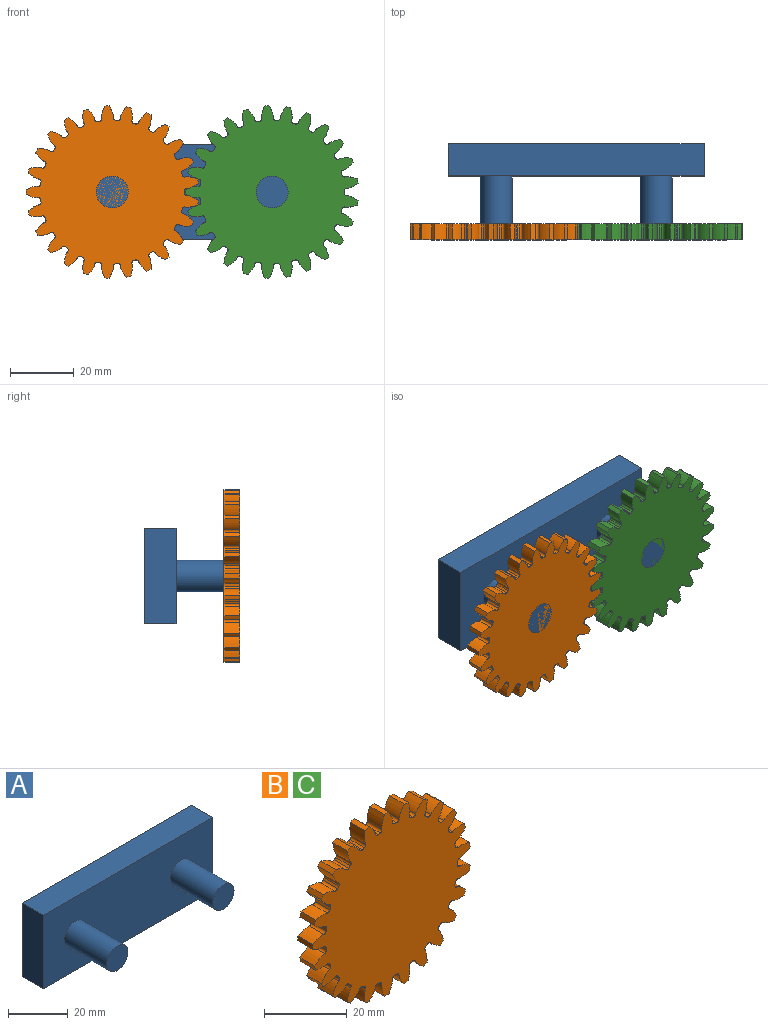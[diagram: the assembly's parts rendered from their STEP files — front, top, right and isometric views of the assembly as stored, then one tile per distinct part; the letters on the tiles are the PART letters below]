
ASSEMBLY  parts=3 mates=2
PART A: 10 faces, bbox 80x30x30 mm
  f0: plane 80x10mm, normal (0,0,1), area 800mm2, adj f1,f3,f4,f5
  f1: plane 30x10mm, normal (-1,0,0), area 300mm2, adj f0,f2,f4,f5
  f2: plane 80x10mm, normal (0,0,-1), area 800mm2, adj f1,f3,f4,f5
  f3: plane 30x10mm, normal (1,0,0), area 300mm2, adj f0,f2,f4,f5
  f4: plane 80x30mm, normal (0,-1,0), area 2242.9mm2, adj f0,f1,f2,f3,f6,f8
  f5: plane 80x30mm, normal (0,1,0), area 2400mm2, adj f0,f1,f2,f3
  f6: cylinder r=5mm len=20mm, axis (0,1,0), area 628.3mm2, adj f4,f7
  f7: plane 10x10mm, normal (0,-1,0), area 78.5mm2, adj f6
  f8: cylinder r=5mm len=20mm, axis (0,1,0), area 628.3mm2, adj f4,f9
  f9: plane 10x10mm, normal (0,-1,0), area 78.5mm2, adj f8
PART B: 152 faces, bbox 53.9x5x54 mm
  f0: cylinder r=27mm len=5mm, axis (0,1,0), area 7.2mm2, adj f24,f26,f137,f149
  f1: cylinder r=27mm len=5mm, axis (0,1,0), area 7.2mm2, adj f24,f26,f144,f147
  f2: cylinder r=27mm len=5mm, axis (0,1,0), area 7.2mm2, adj f24,f26,f132,f139
  f3: cylinder r=27mm len=5mm, axis (0,1,0), area 7.2mm2, adj f24,f26,f127,f134
  f4: cylinder r=27mm len=5mm, axis (0,1,0), area 7.2mm2, adj f24,f26,f122,f129
  f5: cylinder r=27mm len=5mm, axis (0,1,0), area 7.2mm2, adj f24,f26,f112,f124
  f6: cylinder r=27mm len=5mm, axis (0,1,0), area 7.2mm2, adj f24,f26,f107,f119
  f7: cylinder r=27mm len=5mm, axis (0,1,0), area 7.2mm2, adj f24,f26,f114,f117
  f8: cylinder r=27mm len=5mm, axis (0,1,0), area 7.2mm2, adj f24,f26,f102,f109
  f9: cylinder r=27mm len=5mm, axis (0,1,0), area 7.2mm2, adj f24,f26,f97,f104
  f10: cylinder r=27mm len=5mm, axis (0,1,0), area 7.2mm2, adj f24,f26,f92,f99
  f11: cylinder r=27mm len=5mm, axis (0,1,0), area 7.2mm2, adj f24,f26,f77,f94
  f12: cylinder r=27mm len=5mm, axis (0,1,0), area 7.2mm2, adj f24,f26,f27,f89
  f13: cylinder r=27mm len=5mm, axis (0,1,0), area 7.2mm2, adj f24,f26,f84,f87
  f14: cylinder r=27mm len=5mm, axis (0,1,0), area 7.2mm2, adj f24,f26,f72,f79
  f15: cylinder r=27mm len=5mm, axis (0,1,0), area 7.2mm2, adj f24,f26,f74,f82
  f16: cylinder r=27mm len=5mm, axis (0,1,0), area 7.2mm2, adj f24,f26,f69,f142
  f17: cylinder r=27mm len=5mm, axis (0,1,0), area 7.2mm2, adj f24,f26,f64,f67
  f18: cylinder r=27mm len=5mm, axis (0,1,0), area 7.2mm2, adj f24,f26,f59,f62
  f19: cylinder r=27mm len=5mm, axis (0,1,0), area 7.2mm2, adj f24,f26,f54,f57
  f20: cylinder r=27mm len=5mm, axis (0,1,0), area 7.2mm2, adj f24,f26,f42,f49
  f21: cylinder r=27mm len=5mm, axis (0,1,0), area 7.2mm2, adj f24,f26,f32,f44
  f22: cylinder r=27mm len=5mm, axis (0,1,0), area 7.2mm2, adj f24,f26,f39,f52
  f23: cylinder r=27mm len=5mm, axis (0,1,0), area 7.2mm2, adj f24,f26,f34,f37
  f24: plane 53.97x53.87mm, normal (0,-1,0), area 1934.5mm2, adj f0,f1,f2,f3,f4,f5,f6,f7
  f25: cylinder r=27mm len=5mm, axis (0,1,0), area 7.2mm2, adj f24,f26,f29,f47
  f26: plane 53.97x53.87mm, normal (0,1,0), area 1934.5mm2, adj f0,f1,f2,f3,f4,f5,f6,f7
  f27: extruded ~5x3.65mm, area 20.1mm2, adj f12,f24,f26,f30
  f28: cylinder r=22.5mm len=5mm, axis (0,1,0), area 3.4mm2, adj f24,f26,f30,f31
  f29: extruded ~5x3.65mm, area 20.1mm2, adj f24,f25,f26,f31
  f30: cylinder r=0.76mm len=5mm, axis (0,1,0), area 5.8mm2, adj f24,f26,f27,f28
  f31: cylinder r=0.76mm len=5mm, axis (0,1,0), area 5.8mm2, adj f24,f26,f28,f29
  f32: extruded ~5x3.73mm, area 20.1mm2, adj f21,f24,f26,f35
  f33: cylinder r=22.5mm len=5mm, axis (0,1,0), area 3.4mm2, adj f24,f26,f35,f36
  f34: extruded ~5x3.64mm, area 20.1mm2, adj f23,f24,f26,f36
  f35: cylinder r=0.76mm len=5mm, axis (0,1,0), area 5.8mm2, adj f24,f26,f32,f33
  f36: cylinder r=0.76mm len=5mm, axis (0,1,0), area 5.8mm2, adj f24,f26,f33,f34
  f37: extruded ~5x3.27mm, area 20.1mm2, adj f23,f24,f26,f40
  f38: cylinder r=22.5mm len=5mm, axis (0,1,0), area 3.4mm2, adj f24,f26,f40,f41
  f39: extruded ~5x3.92mm, area 20.1mm2, adj f22,f24,f26,f41
  f40: cylinder r=0.76mm len=5mm, axis (0,1,0), area 5.8mm2, adj f24,f26,f37,f38
  f41: cylinder r=0.76mm len=5mm, axis (0,1,0), area 5.8mm2, adj f24,f26,f38,f39
  f42: extruded ~5x3.95mm, area 20.1mm2, adj f20,f24,f26,f45
  f43: cylinder r=22.5mm len=5mm, axis (0,1,0), area 3.4mm2, adj f24,f26,f45,f46
  f44: extruded ~5x3.12mm, area 20.1mm2, adj f21,f24,f26,f46
  f45: cylinder r=0.76mm len=5mm, axis (0,1,0), area 5.8mm2, adj f24,f26,f42,f43
  f46: cylinder r=0.76mm len=5mm, axis (0,1,0), area 5.8mm2, adj f24,f26,f43,f44
  f47: extruded ~5x3.92mm, area 20.1mm2, adj f24,f25,f26,f50
  f48: cylinder r=22.5mm len=5mm, axis (0,1,0), area 3.4mm2, adj f24,f26,f50,f51
  f49: extruded ~5x3.15mm, area 20.1mm2, adj f20,f24,f26,f51
  f50: cylinder r=0.76mm len=5mm, axis (0,1,0), area 5.8mm2, adj f24,f26,f47,f48
  f51: cylinder r=0.76mm len=5mm, axis (0,1,0), area 5.8mm2, adj f24,f26,f48,f49
  f52: extruded ~5x2.99mm, area 20.1mm2, adj f22,f24,f26,f55
  f53: cylinder r=22.5mm len=5mm, axis (0,1,0), area 3.4mm2, adj f24,f26,f55,f56
  f54: extruded ~5x3.95mm, area 20.1mm2, adj f19,f24,f26,f56
  f55: cylinder r=0.76mm len=5mm, axis (0,1,0), area 5.8mm2, adj f24,f26,f52,f53
  f56: cylinder r=0.76mm len=5mm, axis (0,1,0), area 5.8mm2, adj f24,f26,f53,f54
  f57: extruded ~5x3.55mm, area 20.1mm2, adj f19,f24,f26,f60
  f58: cylinder r=22.5mm len=5mm, axis (0,1,0), area 3.4mm2, adj f24,f26,f60,f61
  f59: extruded ~5x3.74mm, area 20.1mm2, adj f18,f24,f26,f61
  f60: cylinder r=0.76mm len=5mm, axis (0,1,0), area 5.8mm2, adj f24,f26,f57,f58
  f61: cylinder r=0.76mm len=5mm, axis (0,1,0), area 5.8mm2, adj f24,f26,f58,f59
  f62: extruded ~5x3.88mm, area 20.1mm2, adj f18,f24,f26,f65
  f63: cylinder r=22.5mm len=5mm, axis (0,1,0), area 3.4mm2, adj f24,f26,f65,f66
  f64: extruded ~5x3.29mm, area 20.1mm2, adj f17,f24,f26,f66
  f65: cylinder r=0.76mm len=5mm, axis (0,1,0), area 5.8mm2, adj f24,f26,f62,f63
  f66: cylinder r=0.76mm len=5mm, axis (0,1,0), area 5.8mm2, adj f24,f26,f63,f64
  f67: extruded ~5x3.97mm, area 20.1mm2, adj f17,f24,f26,f70
  f68: cylinder r=22.5mm len=5mm, axis (0,1,0), area 3.4mm2, adj f24,f26,f70,f71
  f69: extruded ~5x2.96mm, area 20.1mm2, adj f16,f24,f26,f71
  f70: cylinder r=0.76mm len=5mm, axis (0,1,0), area 5.8mm2, adj f24,f26,f67,f68
  f71: cylinder r=0.76mm len=5mm, axis (0,1,0), area 5.8mm2, adj f24,f26,f68,f69
  f72: extruded ~5x3.64mm, area 20.1mm2, adj f14,f24,f26,f75
  f73: cylinder r=22.5mm len=5mm, axis (0,1,0), area 3.4mm2, adj f24,f26,f75,f76
  f74: extruded ~5x3.73mm, area 20.1mm2, adj f15,f24,f26,f76
  f75: cylinder r=0.76mm len=5mm, axis (0,1,0), area 5.8mm2, adj f24,f26,f72,f73
  f76: cylinder r=0.76mm len=5mm, axis (0,1,0), area 5.8mm2, adj f24,f26,f73,f74
  f77: extruded ~5x3.92mm, area 20.1mm2, adj f11,f24,f26,f80
  f78: cylinder r=22.5mm len=5mm, axis (0,1,0), area 3.4mm2, adj f24,f26,f80,f81
  f79: extruded ~5x3.27mm, area 20.1mm2, adj f14,f24,f26,f81
  f80: cylinder r=0.76mm len=5mm, axis (0,1,0), area 5.8mm2, adj f24,f26,f77,f78
  f81: cylinder r=0.76mm len=5mm, axis (0,1,0), area 5.8mm2, adj f24,f26,f78,f79
  f82: extruded ~5x3.12mm, area 20.1mm2, adj f15,f24,f26,f85
  f83: cylinder r=22.5mm len=5mm, axis (0,1,0), area 3.4mm2, adj f24,f26,f85,f86
  f84: extruded ~5x3.95mm, area 20.1mm2, adj f13,f24,f26,f86
  f85: cylinder r=0.76mm len=5mm, axis (0,1,0), area 5.8mm2, adj f24,f26,f82,f83
  f86: cylinder r=0.76mm len=5mm, axis (0,1,0), area 5.8mm2, adj f24,f26,f83,f84
  f87: extruded ~5x3.15mm, area 20.1mm2, adj f13,f24,f26,f90
  f88: cylinder r=22.5mm len=5mm, axis (0,1,0), area 3.4mm2, adj f24,f26,f90,f91
  f89: extruded ~5x3.92mm, area 20.1mm2, adj f12,f24,f26,f91
  f90: cylinder r=0.76mm len=5mm, axis (0,1,0), area 5.8mm2, adj f24,f26,f87,f88
  f91: cylinder r=0.76mm len=5mm, axis (0,1,0), area 5.8mm2, adj f24,f26,f88,f89
  f92: extruded ~5x3.95mm, area 20.1mm2, adj f10,f24,f26,f95
  f93: cylinder r=22.5mm len=5mm, axis (0,1,0), area 3.4mm2, adj f24,f26,f95,f96
  f94: extruded ~5x2.99mm, area 20.1mm2, adj f11,f24,f26,f96
  f95: cylinder r=0.76mm len=5mm, axis (0,1,0), area 5.8mm2, adj f24,f26,f92,f93
  f96: cylinder r=0.76mm len=5mm, axis (0,1,0), area 5.8mm2, adj f24,f26,f93,f94
  f97: extruded ~5x3.74mm, area 20.1mm2, adj f9,f24,f26,f100
  f98: cylinder r=22.5mm len=5mm, axis (0,1,0), area 3.4mm2, adj f24,f26,f100,f101
  f99: extruded ~5x3.55mm, area 20.1mm2, adj f10,f24,f26,f101
  f100: cylinder r=0.76mm len=5mm, axis (0,1,0), area 5.8mm2, adj f24,f26,f97,f98
  f101: cylinder r=0.76mm len=5mm, axis (0,1,0), area 5.8mm2, adj f24,f26,f98,f99
  f102: extruded ~5x3.29mm, area 20.1mm2, adj f8,f24,f26,f105
  f103: cylinder r=22.5mm len=5mm, axis (0,1,0), area 3.4mm2, adj f24,f26,f105,f106
  f104: extruded ~5x3.88mm, area 20.1mm2, adj f9,f24,f26,f106
  f105: cylinder r=0.76mm len=5mm, axis (0,1,0), area 5.8mm2, adj f24,f26,f102,f103
  f106: cylinder r=0.76mm len=5mm, axis (0,1,0), area 5.8mm2, adj f24,f26,f103,f104
  f107: extruded ~5x2.96mm, area 20.1mm2, adj f6,f24,f26,f110
  f108: cylinder r=22.5mm len=5mm, axis (0,1,0), area 3.4mm2, adj f24,f26,f110,f111
  f109: extruded ~5x3.97mm, area 20.1mm2, adj f8,f24,f26,f111
  f110: cylinder r=0.76mm len=5mm, axis (0,1,0), area 5.8mm2, adj f24,f26,f107,f108
  f111: cylinder r=0.76mm len=5mm, axis (0,1,0), area 5.8mm2, adj f24,f26,f108,f109
  f112: extruded ~5x3.87mm, area 20.1mm2, adj f5,f24,f26,f115
  f113: cylinder r=22.5mm len=5mm, axis (0,1,0), area 3.4mm2, adj f24,f26,f115,f116
  f114: extruded ~5x3.41mm, area 20.1mm2, adj f7,f24,f26,f116
  f115: cylinder r=0.76mm len=5mm, axis (0,1,0), area 5.8mm2, adj f24,f26,f112,f113
  f116: cylinder r=0.76mm len=5mm, axis (0,1,0), area 5.8mm2, adj f24,f26,f113,f114
  f117: extruded ~5x3.53mm, area 20.1mm2, adj f7,f24,f26,f120
  f118: cylinder r=22.5mm len=5mm, axis (0,1,0), area 3.4mm2, adj f24,f26,f120,f121
  f119: extruded ~5x3.81mm, area 20.1mm2, adj f6,f24,f26,f121
  f120: cylinder r=0.76mm len=5mm, axis (0,1,0), area 5.8mm2, adj f24,f26,f117,f118
  f121: cylinder r=0.76mm len=5mm, axis (0,1,0), area 5.8mm2, adj f24,f26,f118,f119
  f122: extruded ~5x3.97mm, area 20.1mm2, adj f4,f24,f26,f125
  f123: cylinder r=22.5mm len=5mm, axis (0,1,0), area 3.4mm2, adj f24,f26,f125,f126
  f124: extruded ~5x2.82mm, area 20.1mm2, adj f5,f24,f26,f126
  f125: cylinder r=0.76mm len=5mm, axis (0,1,0), area 5.8mm2, adj f24,f26,f122,f123
  f126: cylinder r=0.76mm len=5mm, axis (0,1,0), area 5.8mm2, adj f24,f26,f123,f124
  f127: extruded ~5x3.82mm, area 20.1mm2, adj f3,f24,f26,f130
  f128: cylinder r=22.5mm len=5mm, axis (0,1,0), area 3.4mm2, adj f24,f26,f130,f131
  f129: extruded ~5x3.43mm, area 20.1mm2, adj f4,f24,f26,f131
  f130: cylinder r=0.76mm len=5mm, axis (0,1,0), area 5.8mm2, adj f24,f26,f127,f128
  f131: cylinder r=0.76mm len=5mm, axis (0,1,0), area 5.8mm2, adj f24,f26,f128,f129
  f132: extruded ~5x3.43mm, area 20.1mm2, adj f2,f24,f26,f135
  f133: cylinder r=22.5mm len=5mm, axis (0,1,0), area 3.4mm2, adj f24,f26,f135,f136
  f134: extruded ~5x3.82mm, area 20.1mm2, adj f3,f24,f26,f136
  f135: cylinder r=0.76mm len=5mm, axis (0,1,0), area 5.8mm2, adj f24,f26,f132,f133
  f136: cylinder r=0.76mm len=5mm, axis (0,1,0), area 5.8mm2, adj f24,f26,f133,f134
  f137: extruded ~5x2.82mm, area 20.1mm2, adj f0,f24,f26,f140
  f138: cylinder r=22.5mm len=5mm, axis (0,1,0), area 3.4mm2, adj f24,f26,f140,f141
  f139: extruded ~5x3.97mm, area 20.1mm2, adj f2,f24,f26,f141
  f140: cylinder r=0.76mm len=5mm, axis (0,1,0), area 5.8mm2, adj f24,f26,f137,f138
  f141: cylinder r=0.76mm len=5mm, axis (0,1,0), area 5.8mm2, adj f24,f26,f138,f139
  f142: extruded ~5x3.81mm, area 20.1mm2, adj f16,f24,f26,f145
  f143: cylinder r=22.5mm len=5mm, axis (0,1,0), area 3.4mm2, adj f24,f26,f145,f146
  f144: extruded ~5x3.53mm, area 20.1mm2, adj f1,f24,f26,f146
  f145: cylinder r=0.76mm len=5mm, axis (0,1,0), area 5.8mm2, adj f24,f26,f142,f143
  f146: cylinder r=0.76mm len=5mm, axis (0,1,0), area 5.8mm2, adj f24,f26,f143,f144
  f147: extruded ~5x3.41mm, area 20.1mm2, adj f1,f24,f26,f150
  f148: cylinder r=22.5mm len=5mm, axis (0,1,0), area 3.4mm2, adj f24,f26,f150,f151
  f149: extruded ~5x3.87mm, area 20.1mm2, adj f0,f24,f26,f151
  f150: cylinder r=0.76mm len=5mm, axis (0,1,0), area 5.8mm2, adj f24,f26,f147,f148
  f151: cylinder r=0.76mm len=5mm, axis (0,1,0), area 5.8mm2, adj f24,f26,f148,f149
PART C: same geometry as B
PLACE A t=(31.52,27.1,-20.89)mm fixed
PLACE B t=(2.25,2.1,66.17)mm
PLACE C t=(52.25,2.1,66.17)mm
MATE revolute C.f0 <-> A.f8  axis (0,-1,0) through (52.25,-2.9,66.17)mm
MATE revolute B.f0 <-> A.f6  axis (0,-1,0) through (2.25,-2.9,66.17)mm
